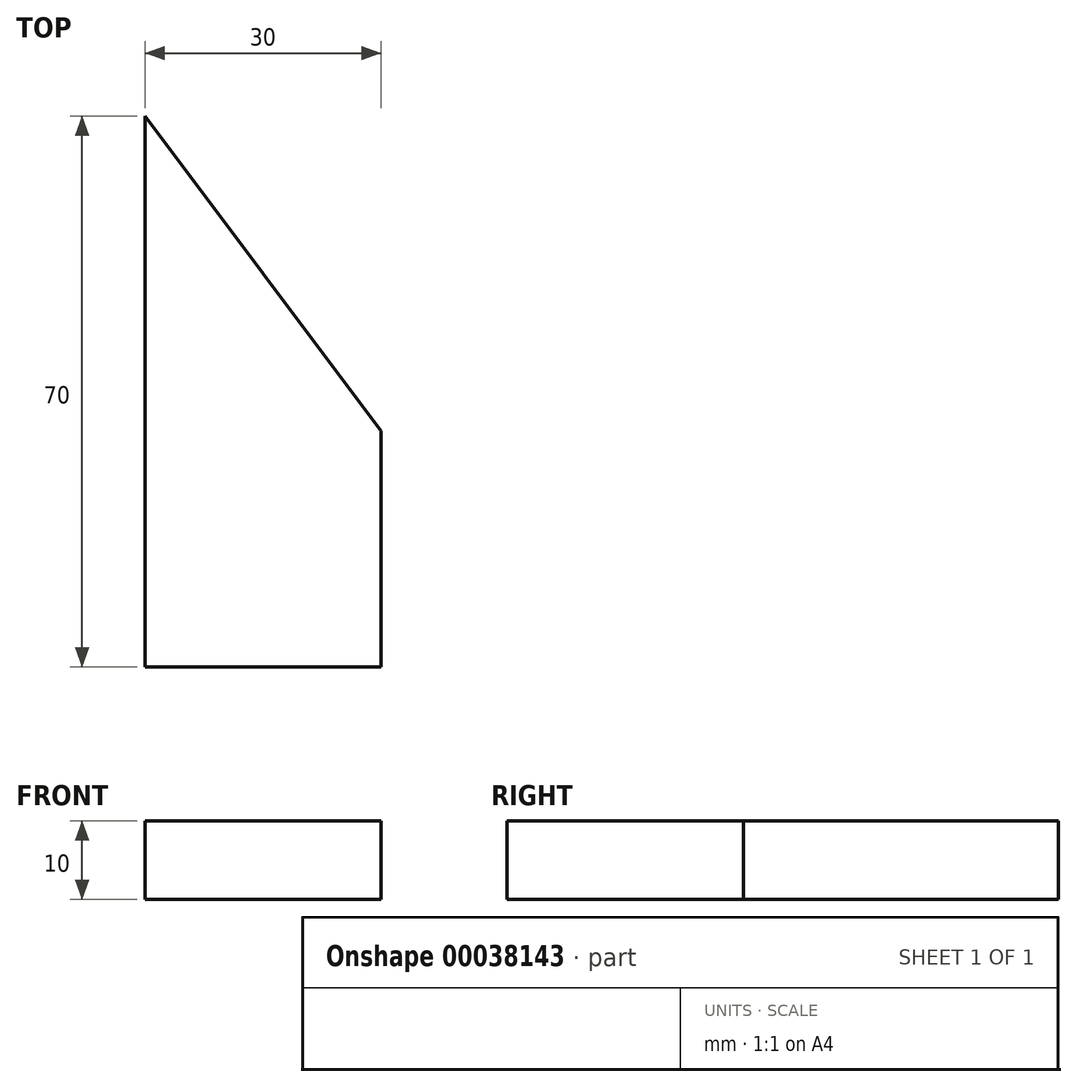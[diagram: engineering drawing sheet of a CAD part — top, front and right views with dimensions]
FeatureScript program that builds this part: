
annotation { "Feature Type Name" : "Feature", "Feature Type Description" : "" }
export const myFeature = defineFeature(function(context is Context, id is Id, definition is map)
    precondition{}
    {
        {
            var Q0;
            Q0=qCreatedBy(makeId("Top.planeOp"),FACE);
            var sketch = newSketch(context, id + "F0", { "sketchPlane" : qUnion([Q0])});
            skLineSegment(sketch, "E0.bottom", {"start": v(-55.65, -35.72) * mm, "end": v(-25.65, -35.72) * mm});
            skLineSegment(sketch, "E0.top", {"start": v(-55.65, -65.72) * mm, "end": v(-25.65, -65.72) * mm});
            skLineSegment(sketch, "E0.left", {"start": v(-55.65, -35.72) * mm, "end": v(-55.65, -65.72) * mm});
            skLineSegment(sketch, "E0.right", {"start": v(-25.65, -35.72) * mm, "end": v(-25.65, -65.72) * mm});
            skLineSegment(sketch, "E1", {"start": v(-55.65, -35.72) * mm, "end": v(-55.65, 4.28) * mm});
            skLineSegment(sketch, "E2", {"start": v(-55.65, 4.28) * mm, "end": v(-25.65, -35.72) * mm});
            skSolve(sketch);
        }
        {
            var Q0;
            Q0 = qSketchRegion(id + "F0", true);
            extrude(context, id + "F1", {"entities" : qUnion([Q0]), "depth" : 10 * mm});
        }
    });
